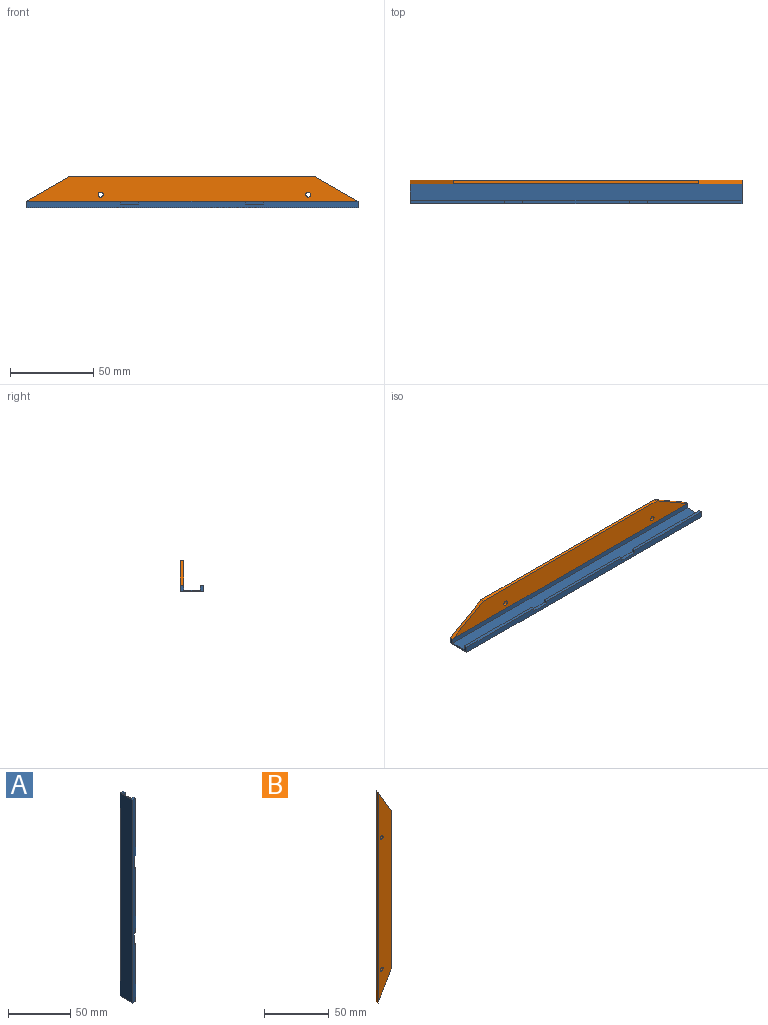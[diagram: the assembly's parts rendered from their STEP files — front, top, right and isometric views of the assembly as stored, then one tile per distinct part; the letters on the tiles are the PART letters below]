
ASSEMBLY  parts=2 mates=1
PART A: 18 faces, bbox 3.8x14x200 mm
  f0: plane 200x3.8mm, normal (0,-1,0), area 720.4mm2, adj f1,f2,f5,f6,f10,f11,f12,f13
  f1: plane 57x2mm, normal (1,0,0), area 114mm2, adj f0,f7,f10,f15
  f2: plane 64x2mm, normal (1,0,0), area 128mm2, adj f0,f7,f12,f16
  f3: plane 200x2mm, normal (1,0,0), area 400mm2, adj f4,f9,f10,f11
  f4: plane 200x3.8mm, normal (0,1,0), area 760mm2, adj f3,f5,f10,f11
  f5: plane 200x14mm, normal (-1,0,0), area 2800mm2, adj f0,f4,f10,f11
  f6: plane 57x2mm, normal (1,0,0), area 114mm2, adj f0,f7,f11,f13
  f7: plane 200x3mm, normal (0,1,0), area 560.4mm2, adj f1,f2,f6,f8,f10,f11,f12,f13
  f8: plane 200x10mm, normal (1,0,0), area 2000mm2, adj f7,f9,f10,f11
  f9: plane 200x3mm, normal (0,-1,0), area 600mm2, adj f3,f8,f10,f11
  f10: plane 14x3.8mm, normal (0,0,1), area 23.2mm2, adj f0,f1,f3,f4,f5,f7,f8,f9
  f11: plane 14x3.8mm, normal (0,0,-1), area 23.2mm2, adj f0,f3,f4,f5,f6,f7,f8,f9
  f12: plane 2x1.8mm, normal (0,0,-1), area 3.6mm2, adj f0,f2,f7,f14
  f13: plane 2x1.8mm, normal (0,0,1), area 3.6mm2, adj f0,f6,f7,f14
  f14: plane 11x2mm, normal (1,0,0), area 22mm2, adj f0,f7,f12,f13
  f15: plane 2x1.8mm, normal (0,0,-1), area 3.6mm2, adj f0,f1,f7,f17
  f16: plane 2x1.8mm, normal (0,0,1), area 3.6mm2, adj f0,f2,f7,f17
  f17: plane 11x2mm, normal (1,0,0), area 22mm2, adj f0,f7,f15,f16
PART B: 8 faces, bbox 15x2x200 mm
  f0: plane 200x15mm, normal (0,1,0), area 2596.2mm2, adj f2,f3,f4,f5,f6,f7
  f1: plane 200x15mm, normal (0,-1,0), area 2596.2mm2, adj f2,f3,f4,f5,f6,f7
  f2: plane 148.04x2mm, normal (1,0,0), area 296.1mm2, adj f0,f1,f6,f7
  f3: plane 200x2mm, normal (-1,0,0), area 400mm2, adj f0,f1,f6,f7
  f4: cylinder r=1.5mm len=3mm, axis (0,1,0), area 18.8mm2, adj f0,f1
  f5: cylinder r=1.5mm len=3mm, axis (0,1,0), area 18.8mm2, adj f0,f1
  f6: plane 25.98x15mm, normal (0.87,0,-0.5), area 60mm2, adj f0,f1,f2,f3
  f7: plane 25.98x15mm, normal (0.87,0,0.5), area 60mm2, adj f0,f1,f2,f3
PLACE A rot(axis=(0,-1,0),90deg) t=(35,0,25)mm
PLACE B rot(axis=(0,-1,0),90deg) t=(35,0,25)mm
MATE fastened B.f3 <-> A.f3  axis (0,0,-1) through (-65,6,25)mm
